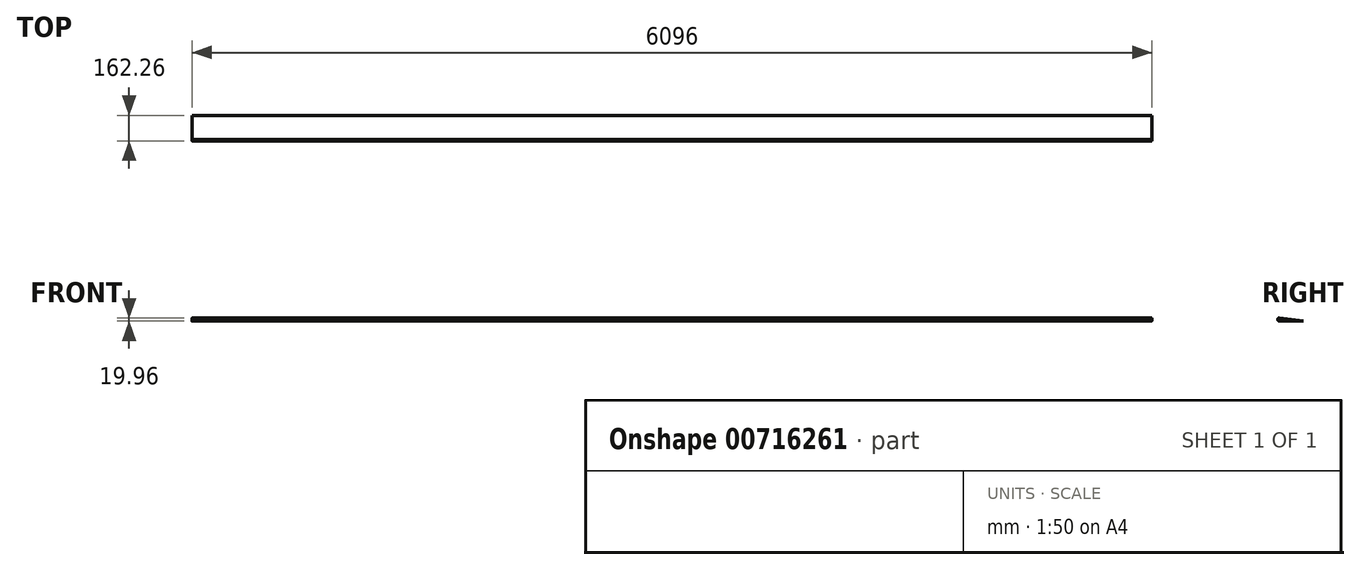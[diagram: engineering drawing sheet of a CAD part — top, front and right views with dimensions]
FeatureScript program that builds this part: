
annotation { "Feature Type Name" : "Feature", "Feature Type Description" : "" }
export const myFeature = defineFeature(function(context is Context, id is Id, definition is map)
    precondition{}
    {
        {
            var Q0;
            Q0=qCreatedBy(makeId("Right.planeOp"),FACE);
            var sketch = newSketch(context, id + "F0", { "sketchPlane" : qUnion([Q0])});
            skLineSegment(sketch, "E0", {"start": v(-76.34, 0) * mm, "end": v(75.72, 0) * mm});
            skArc(sketch, "E1", {"start": v(-76.34, 0) * mm, "mid": v(-83.83, 3.27) * mm, "end": v(-86.5, 11) * mm});
            skArc(sketch, "E2", {"start": v(-86.5, 11) * mm, "mid": v(-83.24, 17.53) * mm, "end": v(-76.34, 19.95) * mm});
            skLineSegment(sketch, "E3", {"start": v(-76.34, 19.95) * mm, "end": v(75.72, 0) * mm});
            skSolve(sketch);
        }
        {
            var Q0;
            Q0 = qSketchRegion(id + "F0", true);
            extrude(context, id + "F1", {"entities" : qUnion([Q0]), "depth" : 6096 * mm, "offsetDistance" : 25.4 * mm});
        }
    });
